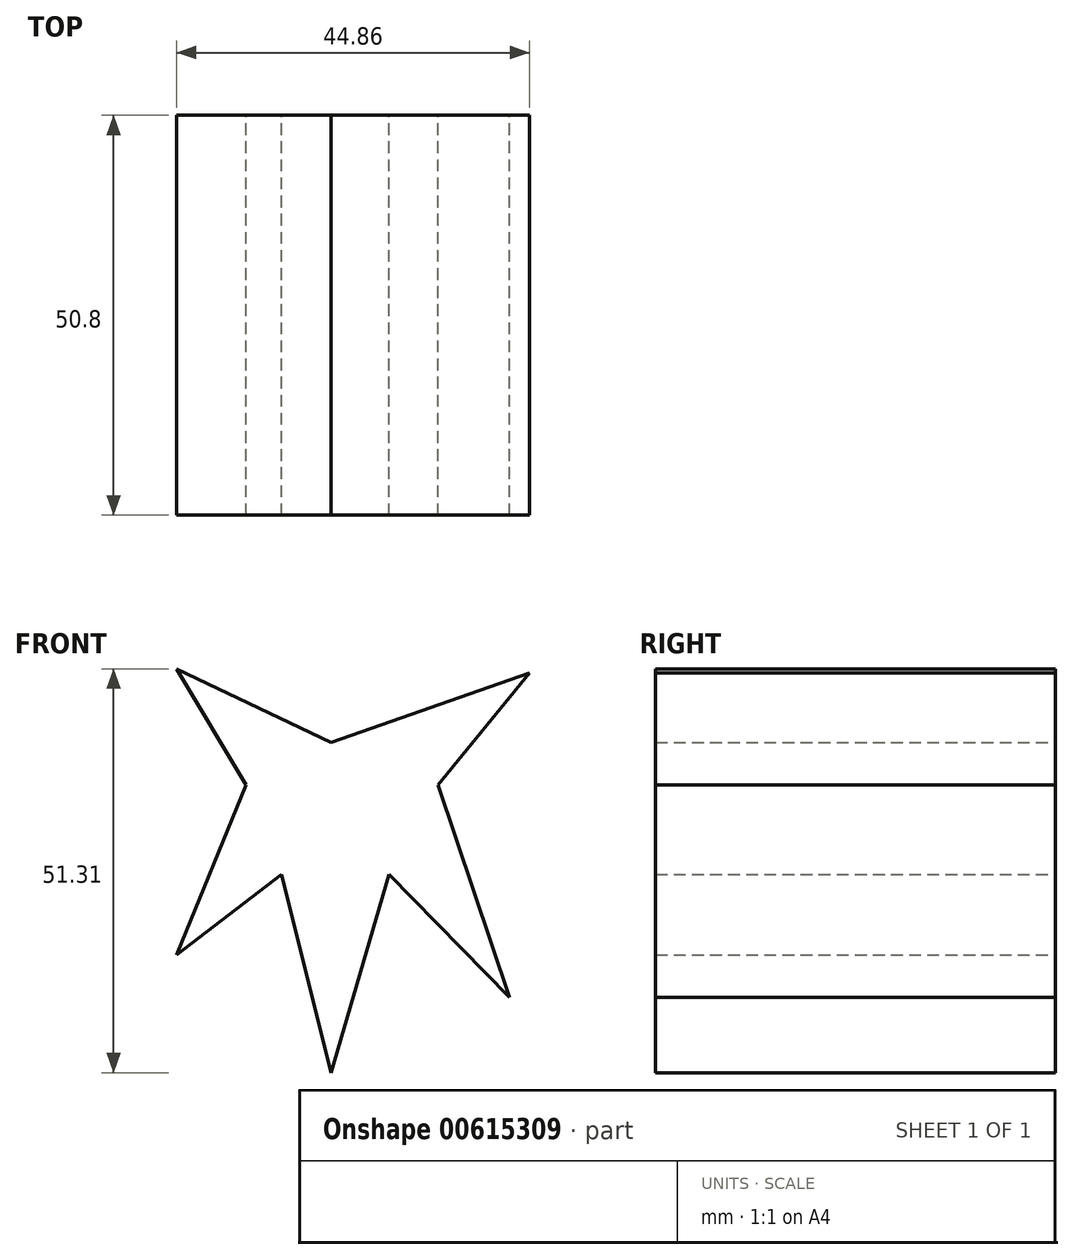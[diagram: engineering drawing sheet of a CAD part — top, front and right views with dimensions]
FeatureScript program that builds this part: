
annotation { "Feature Type Name" : "Feature", "Feature Type Description" : "" }
export const myFeature = defineFeature(function(context is Context, id is Id, definition is map)
    precondition{}
    {
        {
            var Q0;
            Q0=qCreatedBy(makeId("Front.planeOp"),FACE);
            var sketch = newSketch(context, id + "F0", { "sketchPlane" : qUnion([Q0])});
            skLineSegment(sketch, "E0", {"start": v(0, 0) * mm, "end": v(7.35, 25.2) * mm});
            skLineSegment(sketch, "E1", {"start": v(7.35, 25.2) * mm, "end": v(22.68, 9.58) * mm});
            skLineSegment(sketch, "E2", {"start": v(22.68, 9.58) * mm, "end": v(13.6, 36.55) * mm});
            skLineSegment(sketch, "E3", {"start": v(13.6, 36.55) * mm, "end": v(25.24, 50.75) * mm});
            skLineSegment(sketch, "E4", {"start": v(25.24, 50.75) * mm, "end": v(0, 41.94) * mm});
            skLineSegment(sketch, "E5", {"start": v(0, 41.94) * mm, "end": v(-19.62, 51.31) * mm});
            skLineSegment(sketch, "E6", {"start": v(-19.62, 51.31) * mm, "end": v(-10.82, 36.55) * mm});
            skLineSegment(sketch, "E7", {"start": v(-10.82, 36.55) * mm, "end": v(-19.62, 14.97) * mm});
            skLineSegment(sketch, "E8", {"start": v(-19.62, 14.97) * mm, "end": v(-6.28, 25.2) * mm});
            skLineSegment(sketch, "E9", {"start": v(-6.28, 25.2) * mm, "end": v(0, 0) * mm});
            skSolve(sketch);
        }
        {
            var Q0;
            Q0=makeQuery(id+"F0.imprint","IMPRINT",FACE,{"disambiguationData":[TD([[makeQuery(id+"F0.imprint","IMPRINT",EDGE,{"derivedFrom":sQuery(id+"F0.wireOp",EDGE,"E0")}),1.0]])]});
            extrude(context, id + "F1", {"entities" : qUnion([Q0]), "depth" : 50.8 * mm, "offsetDistance" : 25.4 * mm});
        }
        {
            var Q0;
            Q0=makeQuery(id+"F1.opExtrude","CAP_FACE",FACE,{"disambiguationData":[OSD([sQuery(id+"F0.wireOp",EDGE,"E0"),sQuery(id+"F0.wireOp",EDGE,"E1"),sQuery(id+"F0.wireOp",EDGE,"E2"),sQuery(id+"F0.wireOp",EDGE,"E3"),sQuery(id+"F0.wireOp",EDGE,"E4"),sQuery(id+"F0.wireOp",EDGE,"E5"),sQuery(id+"F0.wireOp",EDGE,"E6"),sQuery(id+"F0.wireOp",EDGE,"E7"),sQuery(id+"F0.wireOp",EDGE,"E8"),sQuery(id+"F0.wireOp",EDGE,"E9")])],"isStart":false});
            extrude(context, id + "F2", {"entities" : qUnion([Q0]), "operationType" : NewBodyOperationType.ADD, "oppositeDirection" : true, "depth" : 25.4 * mm, "offsetDistance" : 25.4 * mm});
        }
    });
